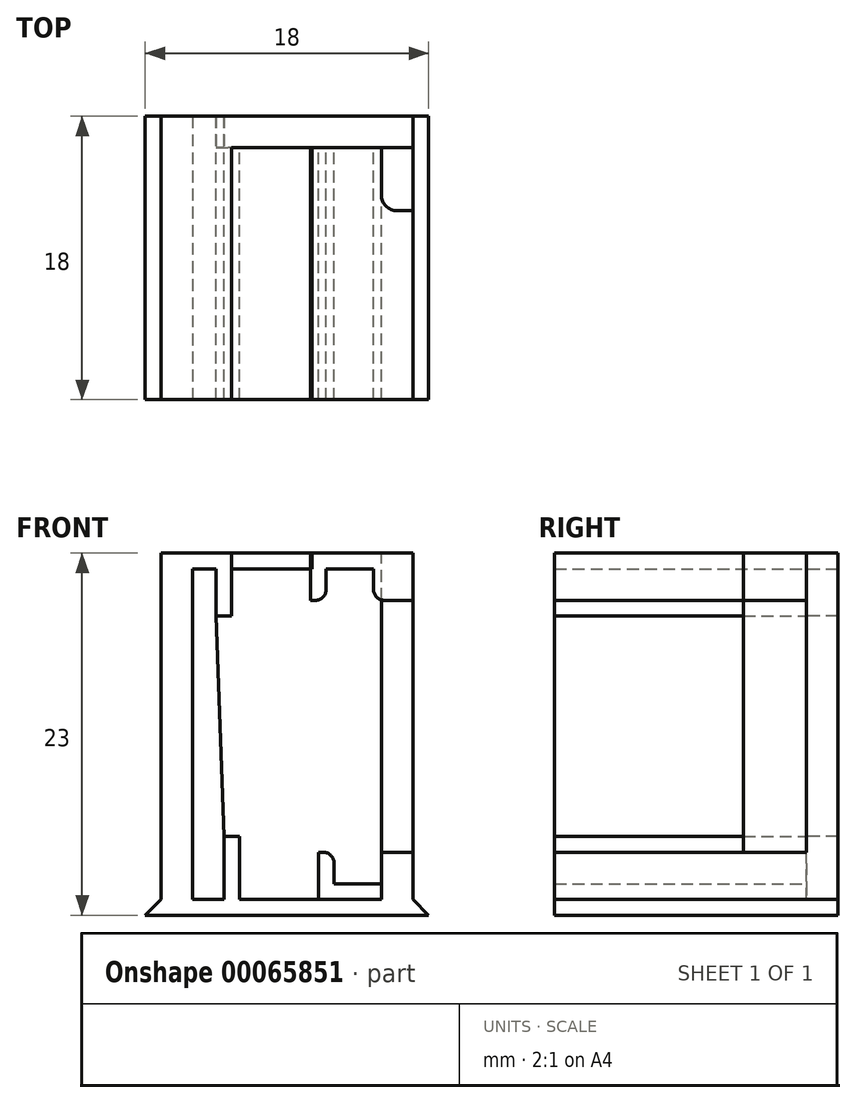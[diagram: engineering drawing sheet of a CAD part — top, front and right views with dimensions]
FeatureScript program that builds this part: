
annotation { "Feature Type Name" : "Feature", "Feature Type Description" : "" }
export const myFeature = defineFeature(function(context is Context, id is Id, definition is map)
    precondition{}
    {
        {
            var Q0;
            Q0=qCreatedBy(makeId("Top.planeOp"),FACE);
            var sketch = newSketch(context, id + "F0", { "sketchPlane" : qUnion([Q0])});
            skLineSegment(sketch, "E0.bottom", {"start": v(9, -10.06) * mm, "end": v(-9, -10.06) * mm});
            skLineSegment(sketch, "E0.left", {"start": v(9, -10.06) * mm, "end": v(9, 7.94) * mm});
            skLineSegment(sketch, "E0.right", {"start": v(-9, -10.06) * mm, "end": v(-9, 7.94) * mm});
            skPoint(sketch, "E0.middle", {"position": v(0, 0) * mm});
            skPoint(sketch, "E1.orphan", {"position": v(-9, 10.06) * mm});
            skPoint(sketch, "E2.orphan", {"position": v(9, 10.06) * mm});
            skLineSegment(sketch, "E3", {"start": v(9, 7.94) * mm, "end": v(-9, 7.94) * mm});
            skSolve(sketch);
        }
        {
            var Q0;
            Q0 = qSketchRegion(id + "F0", true);
            extrude(context, id + "F1", {"entities" : qUnion([Q0]), "depth" : 1 * mm});
        }
        {
            var Q0;
            Q0=makeQuery(id+"F1.opExtrude","CAP_FACE",FACE,{"disambiguationData":[OSD([sQuery(id+"F0.wireOp",EDGE,"E0.bottom"),sQuery(id+"F0.wireOp",EDGE,"E0.top"),sQuery(id+"F0.wireOp",EDGE,"E0.left"),sQuery(id+"F0.wireOp",EDGE,"E0.right")])],"isStart":false});
            var sketch = newSketch(context, id + "F2", { "sketchPlane" : qUnion([Q0])});
            skLineSegment(sketch, "E4.bottom", {"start": v(8, -10.06) * mm, "end": v(-8, -10.06) * mm});
            skLineSegment(sketch, "E4.top", {"start": v(8, 7.94) * mm, "end": v(-8, 7.94) * mm});
            skLineSegment(sketch, "E4.left", {"start": v(8, -10.06) * mm, "end": v(8, 7.94) * mm});
            skLineSegment(sketch, "E4.right", {"start": v(-8, -10.06) * mm, "end": v(-8, 7.94) * mm});
            skPoint(sketch, "E4.middle", {"position": v(0, -1.06) * mm});
            skLineSegment(sketch, "E5.bottom", {"start": v(-6, 5.94) * mm, "end": v(6, 5.94) * mm});
            skLineSegment(sketch, "E5.top", {"start": v(-6, -10.06) * mm, "end": v(6, -10.06) * mm});
            skLineSegment(sketch, "E5.left", {"start": v(-6, 5.94) * mm, "end": v(-6, -10.06) * mm});
            skLineSegment(sketch, "E5.right", {"start": v(6, 5.94) * mm, "end": v(6, -10.06) * mm});
            skSolve(sketch);
        }
        {
            var Q0;
            Q0=makeQuery(id+"F2.imprint","IMPRINT",FACE,{"disambiguationData":[TD([[makeQuery(id+"F2.imprint","IMPRINT",EDGE,{"derivedFrom":sQuery(id+"F2.wireOp",EDGE,"E4.top")}),1.0]])]});
            extrude(context, id + "F3", {"entities" : qUnion([Q0]), "operationType" : NewBodyOperationType.ADD, "depth" : 22 * mm});
        }
        {
            var Q0;
            {var subQ0=sQuery(id+"F2.wireOp",EDGE,"E4.bottom");var subQ1=sQuery(id+"F0.wireOp",EDGE,"E0.bottom");var subQ2=makeQuery(id+"F1.opExtrude","CAP_EDGE",EDGE,{"disambiguationData":[OSD([subQ1])],"isStart":false});Q0=makeQuery(id+"F3.boolean.opBoolean","MERGE",FACE,{"derivedFrom":[makeQuery(id+"F1.opExtrude","SWEPT_FACE",FACE,{"disambiguationData":[OSD([subQ1])]}),makeQuery(id+"F3.opExtrude","SWEPT_FACE",FACE,{"disambiguationData":[OSD([subQ0]),TDD([makeQuery(id+"F2.imprint","IMPRINT",EDGE,{"disambiguationData":[TD([[makeQuery(id+"F2.imprint","INTERSECT",VERTEX,{"derivedFrom":[subQ2,subQ0,sQuery(id+"F2.wireOp",EDGE,"E4.left")]}),-1.0]])],"derivedFrom":subQ0})])]}),makeQuery(id+"F3.opExtrude","SWEPT_FACE",FACE,{"disambiguationData":[OSD([subQ0]),TDD([makeQuery(id+"F2.imprint","IMPRINT",EDGE,{"disambiguationData":[TD([[makeQuery(id+"F2.imprint","INTERSECT",VERTEX,{"derivedFrom":[subQ2,subQ0,sQuery(id+"F2.wireOp",EDGE,"E4.right")]}),1.0]])],"derivedFrom":subQ0})])]})]});}
            var sketch = newSketch(context, id + "F4", { "sketchPlane" : qUnion([Q0])});
            skLineSegment(sketch, "E6", {"start": v(-9, 0) * mm, "end": v(-8, 1) * mm});
            skLineSegment(sketch, "E7", {"start": v(9, 0) * mm, "end": v(8, 1) * mm});
            skSolve(sketch);
        }
        {
            var Q0;
            Q0=makeQuery(id+"F4.imprint","IMPRINT",FACE,{"disambiguationData":[TD([[makeQuery(id+"F4.imprint","IMPRINT",EDGE,{"derivedFrom":sQuery(id+"F4.wireOp",EDGE,"E6")}),1.0]])]});
            var Q1;
            Q1=makeQuery(id+"F1.opExtrude","CAP_EDGE",EDGE,{"disambiguationData":[OSD([sQuery(id+"F0.wireOp",EDGE,"E0.right")])],"isStart":true});
            sweep(context, id + "F5", {"operationType" : NewBodyOperationType.REMOVE, "profiles" : qUnion([Q0]), "path" : qUnion([Q1])});
        }
        {
            var Q0;
            {var subQ0=sQuery(id+"F2.wireOp",EDGE,"E4.bottom");var subQ1=sQuery(id+"F0.wireOp",EDGE,"E0.bottom");var subQ2=makeQuery(id+"F1.opExtrude","CAP_EDGE",EDGE,{"disambiguationData":[OSD([subQ1])],"isStart":false});Q0=makeQuery(id+"F3.boolean.opBoolean","MERGE",FACE,{"derivedFrom":[makeQuery(id+"F1.opExtrude","SWEPT_FACE",FACE,{"disambiguationData":[OSD([subQ1])]}),makeQuery(id+"F3.opExtrude","SWEPT_FACE",FACE,{"disambiguationData":[OSD([subQ0]),TDD([makeQuery(id+"F2.imprint","IMPRINT",EDGE,{"disambiguationData":[TD([[makeQuery(id+"F2.imprint","INTERSECT",VERTEX,{"derivedFrom":[subQ2,subQ0,sQuery(id+"F2.wireOp",EDGE,"E4.left")]}),-1.0]])],"derivedFrom":subQ0})])]}),makeQuery(id+"F3.opExtrude","SWEPT_FACE",FACE,{"disambiguationData":[OSD([subQ0]),TDD([makeQuery(id+"F2.imprint","IMPRINT",EDGE,{"disambiguationData":[TD([[makeQuery(id+"F2.imprint","INTERSECT",VERTEX,{"derivedFrom":[subQ2,subQ0,sQuery(id+"F2.wireOp",EDGE,"E4.right")]}),1.0]])],"derivedFrom":subQ0})])]})]});}
            var sketch = newSketch(context, id + "F6", { "sketchPlane" : qUnion([Q0])});
            skLineSegment(sketch, "E8", {"start": v(6, 4) * mm, "end": v(8, 4) * mm});
            skSolve(sketch);
        }
        {
            var Q0;
            Q0 = qSketchRegion(id + "F6", true);
            var Q1;
            {var subQ0=sQuery(id+"F6.wireOp",EDGE,"E8");Q1=makeQuery(id+"F6.imprint","IMPRINT",FACE,{"disambiguationData":[TD([[makeQuery(id+"F6.imprint","IMPRINT",EDGE,{"derivedFrom":subQ0}),1.0]])]});}
            var Q2;
            Q2=makeQuery(id+"F3.opExtrude","SWEPT_FACE",FACE,{"disambiguationData":[OSD([sQuery(id+"F2.wireOp",EDGE,"E5.bottom")])]});
            extrude(context, id + "F7", {"entities" : qUnion([Q0, Q1]), "operationType" : NewBodyOperationType.REMOVE, "endBound" : BoundingType.UP_TO_SURFACE, "oppositeDirection" : true, "endBoundEntityFace" : qUnion([Q2]), "depth" : 25 * mm});
        }
        {
            var Q0;
            Q0=makeQuery(id+"F7.boolean.opBoolean","MERGE",FACE,{"derivedFrom":[makeQuery(id+"F3.opExtrude","SWEPT_FACE",FACE,{"disambiguationData":[OSD([sQuery(id+"F2.wireOp",EDGE,"E5.bottom")])]})],"fromTools":[makeQuery(id+"F7.opExtrude","CAP_FACE",FACE,{"disambiguationData":[OSD([sQuery(id+"F0.wireOp",EDGE,"E0.bottom"),sQuery(id+"F2.wireOp",EDGE,"E4.bottom"),sQuery(id+"F2.wireOp",EDGE,"E4.left"),sQuery(id+"F2.wireOp",EDGE,"E5.top"),sQuery(id+"F2.wireOp",EDGE,"E5.right"),sQuery(id+"F6.wireOp",EDGE,"E8")])],"isStart":false})]});
            var sketch = newSketch(context, id + "F8", { "sketchPlane" : qUnion([Q0])});
            skLineSegment(sketch, "E9.bottom", {"start": v(-6, 23) * mm, "end": v(-3.5, 23) * mm});
            skLineSegment(sketch, "E9.top", {"start": v(-6, 19) * mm, "end": v(-6, 19) * mm});
            skLineSegment(sketch, "E9.left", {"start": v(-6, 23) * mm, "end": v(-6, 19) * mm});
            skLineSegment(sketch, "E9.right", {"start": v(-3.5, 23) * mm, "end": v(-3.5, 19) * mm});
            skLineSegment(sketch, "E10.top", {"start": v(-6, 22) * mm, "end": v(-4.5, 22) * mm});
            skLineSegment(sketch, "E10.left", {"start": v(-6, 19) * mm, "end": v(-6, 22) * mm});
            skLineSegment(sketch, "E10.right", {"start": v(-4.5, 19) * mm, "end": v(-4.5, 22) * mm});
            skLineSegment(sketch, "E11.bottom", {"start": v(-3, 1) * mm, "end": v(-5.5, 1) * mm});
            skLineSegment(sketch, "E11.top", {"start": v(-3, 5) * mm, "end": v(-4, 5) * mm});
            skLineSegment(sketch, "E11.left", {"start": v(-3, 1) * mm, "end": v(-3, 5) * mm});
            skLineSegment(sketch, "E11.right", {"start": v(-5.5, 1) * mm, "end": v(-5.5, 5) * mm});
            skLineSegment(sketch, "E12.top", {"start": v(-4, 1) * mm, "end": v(-5.5, 1) * mm});
            skLineSegment(sketch, "E12.left", {"start": v(-4, 5.19) * mm, "end": v(-4, 1) * mm});
            skLineSegment(sketch, "E12.right", {"start": v(-5.5, 5) * mm, "end": v(-5.5, 1) * mm});
            skLineSegment(sketch, "E13.trimOffspring", {"start": v(-5.5, 5) * mm, "end": v(-5.5, 5) * mm});
            skLineSegment(sketch, "E14.trimOffspring", {"start": v(-4.5, 19) * mm, "end": v(-3.5, 19) * mm});
            skPoint(sketch, "E12.bottom.start.orphan", {"position": v(-4.25, 5) * mm});
            skLineSegment(sketch, "E15", {"start": v(-4, 5.19) * mm, "end": v(-4, 5) * mm});
            skSolve(sketch);
        }
        {
            var Q0;
            Q0=makeQuery(id+"F8.imprint","IMPRINT",FACE,{"disambiguationData":[TD([[makeQuery(id+"F8.imprint","IMPRINT",EDGE,{"derivedFrom":sQuery(id+"F8.wireOp",EDGE,"E9.bottom")}),-1.0]])]});
            var Q1;
            Q1=makeQuery(id+"F8.imprint","IMPRINT",FACE,{"disambiguationData":[TD([[makeQuery(id+"F8.imprint","IMPRINT",EDGE,{"derivedFrom":sQuery(id+"F8.wireOp",EDGE,"E11.bottom")}),1.0]])]});
            var Q2;
            {var subQ0=sQuery(id+"F2.wireOp",EDGE,"E4.bottom");var subQ1=sQuery(id+"F0.wireOp",EDGE,"E0.bottom");var subQ2=makeQuery(id+"F1.opExtrude","CAP_EDGE",EDGE,{"disambiguationData":[OSD([subQ1])],"isStart":false});Q2=makeQuery(id+"F3.boolean.opBoolean","MERGE",FACE,{"derivedFrom":[makeQuery(id+"F1.opExtrude","SWEPT_FACE",FACE,{"disambiguationData":[OSD([subQ1])]}),makeQuery(id+"F3.opExtrude","SWEPT_FACE",FACE,{"disambiguationData":[OSD([subQ0]),TDD([makeQuery(id+"F2.imprint","IMPRINT",EDGE,{"disambiguationData":[TD([[makeQuery(id+"F2.imprint","INTERSECT",VERTEX,{"derivedFrom":[subQ2,subQ0,sQuery(id+"F2.wireOp",EDGE,"E4.left")]}),-1.0]])],"derivedFrom":subQ0})])]}),makeQuery(id+"F3.opExtrude","SWEPT_FACE",FACE,{"disambiguationData":[OSD([subQ0]),TDD([makeQuery(id+"F2.imprint","IMPRINT",EDGE,{"disambiguationData":[TD([[makeQuery(id+"F2.imprint","INTERSECT",VERTEX,{"derivedFrom":[subQ2,subQ0,sQuery(id+"F2.wireOp",EDGE,"E4.right")]}),1.0]])],"derivedFrom":subQ0})])]})]});}
            extrude(context, id + "F9", {"entities" : qUnion([Q0, Q1]), "operationType" : NewBodyOperationType.ADD, "endBound" : BoundingType.UP_TO_SURFACE, "endBoundEntityFace" : qUnion([Q2]), "depth" : 25 * mm});
        }
        {
            var Q0;
            Q0=makeQuery(id+"F4.imprint","IMPRINT",FACE,{"disambiguationData":[TD([[makeQuery(id+"F4.imprint","IMPRINT",EDGE,{"derivedFrom":sQuery(id+"F4.wireOp",EDGE,"E7")}),-1.0]])]});
            extrude(context, id + "F10", {"entities" : qUnion([Q0]), "operationType" : NewBodyOperationType.REMOVE, "oppositeDirection" : true, "depth" : 25 * mm});
        }
        {
            var Q0;
            Q0=makeQuery(id+"F7.boolean.opBoolean","MERGE",FACE,{"derivedFrom":[makeQuery(id+"F3.opExtrude","SWEPT_FACE",FACE,{"disambiguationData":[OSD([sQuery(id+"F2.wireOp",EDGE,"E5.bottom")])]})],"fromTools":[makeQuery(id+"F7.opExtrude","CAP_FACE",FACE,{"disambiguationData":[OSD([sQuery(id+"F0.wireOp",EDGE,"E0.bottom"),sQuery(id+"F2.wireOp",EDGE,"E4.bottom"),sQuery(id+"F2.wireOp",EDGE,"E4.left"),sQuery(id+"F2.wireOp",EDGE,"E5.top"),sQuery(id+"F2.wireOp",EDGE,"E5.right"),sQuery(id+"F6.wireOp",EDGE,"E8")])],"isStart":false})]});
            var sketch = newSketch(context, id + "F11", { "sketchPlane" : qUnion([Q0])});
            skLineSegment(sketch, "E16.bottom", {"start": v(6, 1) * mm, "end": v(2, 1) * mm});
            skLineSegment(sketch, "E16.top", {"start": v(6, 4) * mm, "end": v(6, 4) * mm});
            skLineSegment(sketch, "E16.left", {"start": v(6, 1) * mm, "end": v(6, 4) * mm});
            skLineSegment(sketch, "E16.right", {"start": v(2, 1) * mm, "end": v(2, 4) * mm});
            skLineSegment(sketch, "E17.top", {"start": v(3, 2) * mm, "end": v(6, 2) * mm});
            skLineSegment(sketch, "E17.left", {"start": v(3, 4) * mm, "end": v(3, 2) * mm});
            skLineSegment(sketch, "E17.right", {"start": v(6, 4) * mm, "end": v(6, 2) * mm});
            skLineSegment(sketch, "E18.bottom", {"start": v(5.5, 23) * mm, "end": v(1.5, 23) * mm});
            skLineSegment(sketch, "E18.top", {"start": v(5.5, 20) * mm, "end": v(5.5, 20) * mm});
            skLineSegment(sketch, "E18.left", {"start": v(5.5, 22) * mm, "end": v(5.5, 20) * mm});
            skLineSegment(sketch, "E18.right", {"start": v(1.5, 23) * mm, "end": v(1.5, 20) * mm});
            skLineSegment(sketch, "E19.top", {"start": v(2.5, 22) * mm, "end": v(5.5, 22) * mm});
            skLineSegment(sketch, "E19.left", {"start": v(2.5, 20) * mm, "end": v(2.5, 22) * mm});
            skLineSegment(sketch, "E19.right", {"start": v(5.5, 20) * mm, "end": v(5.5, 22) * mm});
            skLineSegment(sketch, "E20.trimOffspring", {"start": v(2.5, 20) * mm, "end": v(1.5, 20) * mm});
            skLineSegment(sketch, "E21.trimOffspring", {"start": v(3, 4) * mm, "end": v(2, 4) * mm});
            skLineSegment(sketch, "E22", {"start": v(5.5, 20) * mm, "end": v(8, 20) * mm});
            skLineSegment(sketch, "E23", {"start": v(1.5, 23) * mm, "end": v(8, 23) * mm});
            skLineSegment(sketch, "E24", {"start": v(8, 23) * mm, "end": v(8, 20) * mm});
            skSolve(sketch);
        }
        {
            var Q0;
            Q0 = qSketchRegion(id + "F11", true);
            var Q1;
            {var subQ0=sQuery(id+"F2.wireOp",EDGE,"E4.bottom");var subQ1=sQuery(id+"F0.wireOp",EDGE,"E0.bottom");var subQ2=makeQuery(id+"F1.opExtrude","CAP_EDGE",EDGE,{"disambiguationData":[OSD([subQ1])],"isStart":false});Q1=makeQuery(id+"F3.boolean.opBoolean","MERGE",FACE,{"derivedFrom":[makeQuery(id+"F1.opExtrude","SWEPT_FACE",FACE,{"disambiguationData":[OSD([subQ1])]}),makeQuery(id+"F3.opExtrude","SWEPT_FACE",FACE,{"disambiguationData":[OSD([subQ0]),TDD([makeQuery(id+"F2.imprint","IMPRINT",EDGE,{"disambiguationData":[TD([[makeQuery(id+"F2.imprint","INTERSECT",VERTEX,{"derivedFrom":[subQ2,subQ0,sQuery(id+"F2.wireOp",EDGE,"E4.left")]}),-1.0]])],"derivedFrom":subQ0})])]}),makeQuery(id+"F3.opExtrude","SWEPT_FACE",FACE,{"disambiguationData":[OSD([subQ0]),TDD([makeQuery(id+"F2.imprint","IMPRINT",EDGE,{"disambiguationData":[TD([[makeQuery(id+"F2.imprint","INTERSECT",VERTEX,{"derivedFrom":[subQ2,subQ0,sQuery(id+"F2.wireOp",EDGE,"E4.right")]}),1.0]])],"derivedFrom":subQ0})])]})]});}
            extrude(context, id + "F12", {"entities" : qUnion([Q0]), "endBound" : BoundingType.UP_TO_SURFACE, "endBoundEntityFace" : qUnion([Q1]), "depth" : 20 * mm});
        }
        {
            var Q0;
            Q0=makeQuery(id+"F7.boolean.opBoolean","MERGE",FACE,{"derivedFrom":[makeQuery(id+"F3.opExtrude","SWEPT_FACE",FACE,{"disambiguationData":[OSD([sQuery(id+"F2.wireOp",EDGE,"E5.bottom")])]})],"fromTools":[makeQuery(id+"F7.opExtrude","CAP_FACE",FACE,{"disambiguationData":[OSD([sQuery(id+"F0.wireOp",EDGE,"E0.bottom"),sQuery(id+"F2.wireOp",EDGE,"E4.bottom"),sQuery(id+"F2.wireOp",EDGE,"E4.left"),sQuery(id+"F2.wireOp",EDGE,"E5.top"),sQuery(id+"F2.wireOp",EDGE,"E5.right"),sQuery(id+"F6.wireOp",EDGE,"E8")])],"isStart":false})]});
            var sketch = newSketch(context, id + "F13", { "sketchPlane" : qUnion([Q0])});
            skLineSegment(sketch, "E25.bottom", {"start": v(8, 4) * mm, "end": v(6, 4) * mm});
            skLineSegment(sketch, "E25.top", {"start": v(8, 23) * mm, "end": v(6, 23) * mm});
            skLineSegment(sketch, "E25.left", {"start": v(8, 4) * mm, "end": v(8, 23) * mm});
            skLineSegment(sketch, "E25.right", {"start": v(6, 4) * mm, "end": v(6, 23) * mm});
            skSolve(sketch);
        }
        {
            var Q0;
            Q0 = qSketchRegion(id + "F13", true);
            extrude(context, id + "F14", {"entities" : qUnion([Q0]), "depth" : 2 * mm});
        }
        {
            var Q0;
            Q0=makeQuery(id+"F14.opExtrude","SWEPT_BODY",BODY,{"disambiguationData":[OSD([sQuery(id+"F13.wireOp",EDGE,"E25.bottom"),sQuery(id+"F13.wireOp",EDGE,"E25.top"),sQuery(id+"F13.wireOp",EDGE,"E25.left"),sQuery(id+"F13.wireOp",EDGE,"E25.right")])]});
            deleteBodies(context, id + "F15", {"entities" : qUnion([Q0])});
        }
        {
            var Q0;
            Q0 = qSketchRegion(id + "F13", true);
            extrude(context, id + "F16", {"entities" : qUnion([Q0]), "depth" : 4 * mm});
        }
        {
            var Q0;
            Q0=makeQuery(id+"F7.boolean.opBoolean","COPY",EDGE,{"derivedFrom":makeQuery(id+"F7.opExtrude","SWEPT_EDGE",EDGE,{"disambiguationData":[OSD([sQuery(id+"F2.wireOp",EDGE,"E4.bottom"),sQuery(id+"F2.wireOp",EDGE,"E5.top"),sQuery(id+"F2.wireOp",EDGE,"E5.right"),sQuery(id+"F6.wireOp",EDGE,"E8")])]})});
            var Q1;
            Q1=makeQuery(id+"F12.opExtrude","SWEPT_EDGE",EDGE,{"disambiguationData":[OSD([sQuery(id+"F11.wireOp",EDGE,"E17.left"),sQuery(id+"F11.wireOp",EDGE,"E21.trimOffspring")])]});
            var Q2;
            Q2=makeQuery(id+"F12.opExtrude","SWEPT_EDGE",EDGE,{"disambiguationData":[OSD([sQuery(id+"F11.wireOp",EDGE,"E19.left"),sQuery(id+"F11.wireOp",EDGE,"E20.trimOffspring")])]});
            var Q3;
            Q3=makeQuery(id+"F12.opExtrude","SWEPT_EDGE",EDGE,{"disambiguationData":[OSD([sQuery(id+"F11.wireOp",EDGE,"E19.right"),sQuery(id+"F11.wireOp",EDGE,"E22")])]});
            fillet(context, id + "F17", {"entities" : qUnion([Q0, Q1, Q2, Q3]), "radius" : .7 * mm, "tangentPropagation" : true, "allowEdgeOverflow" : false});
        }
        {
            var Q0;
            Q0=makeQuery(id+"F16.opExtrude","CAP_EDGE",EDGE,{"disambiguationData":[OSD([sQuery(id+"F13.wireOp",EDGE,"E25.right")])],"isStart":false});
            fillet(context, id + "F18", {"entities" : qUnion([Q0]), "radius" : 1 * mm, "tangentPropagation" : true, "allowEdgeOverflow" : false});
        }
        {
            var Q0;
            Q0=makeQuery(id+"F7.boolean.opBoolean","MERGE",FACE,{"derivedFrom":[makeQuery(id+"F3.opExtrude","SWEPT_FACE",FACE,{"disambiguationData":[OSD([sQuery(id+"F2.wireOp",EDGE,"E5.bottom")])]})],"fromTools":[makeQuery(id+"F7.opExtrude","CAP_FACE",FACE,{"disambiguationData":[OSD([sQuery(id+"F0.wireOp",EDGE,"E0.bottom"),sQuery(id+"F2.wireOp",EDGE,"E4.bottom"),sQuery(id+"F2.wireOp",EDGE,"E4.left"),sQuery(id+"F2.wireOp",EDGE,"E5.top"),sQuery(id+"F2.wireOp",EDGE,"E5.right"),sQuery(id+"F6.wireOp",EDGE,"E8")])],"isStart":false})]});
            var sketch = newSketch(context, id + "F19", { "sketchPlane" : qUnion([Q0])});
            skLineSegment(sketch, "E26", {"start": v(-3.5, 22) * mm, "end": v(1.6, 22) * mm});
            skLineSegment(sketch, "E27.bottom", {"start": v(-3.5, 23) * mm, "end": v(1.6, 23) * mm});
            skLineSegment(sketch, "E27.left", {"start": v(-3.5, 23) * mm, "end": v(-3.5, 22) * mm});
            skLineSegment(sketch, "E27.right", {"start": v(1.6, 23) * mm, "end": v(1.6, 22) * mm});
            skSolve(sketch);
        }
        {
            var Q0;
            Q0 = qSketchRegion(id + "F19", true);
            var Q1;
            {var subQ0=sQuery(id+"F2.wireOp",EDGE,"E4.bottom");var subQ1=sQuery(id+"F0.wireOp",EDGE,"E0.bottom");var subQ2=makeQuery(id+"F1.opExtrude","CAP_EDGE",EDGE,{"disambiguationData":[OSD([subQ1])],"isStart":false});Q1=makeQuery(id+"F9.boolean.opBoolean","MERGE",FACE,{"derivedFrom":[makeQuery(id+"F3.boolean.opBoolean","MERGE",FACE,{"derivedFrom":[makeQuery(id+"F1.opExtrude","SWEPT_FACE",FACE,{"disambiguationData":[OSD([subQ1])]}),makeQuery(id+"F3.opExtrude","SWEPT_FACE",FACE,{"disambiguationData":[OSD([subQ0]),TDD([makeQuery(id+"F2.imprint","IMPRINT",EDGE,{"disambiguationData":[TD([[makeQuery(id+"F2.imprint","INTERSECT",VERTEX,{"derivedFrom":[subQ2,subQ0,sQuery(id+"F2.wireOp",EDGE,"E4.left")]}),-1.0]])],"derivedFrom":subQ0})])]}),makeQuery(id+"F3.opExtrude","SWEPT_FACE",FACE,{"disambiguationData":[OSD([subQ0]),TDD([makeQuery(id+"F2.imprint","IMPRINT",EDGE,{"disambiguationData":[TD([[makeQuery(id+"F2.imprint","INTERSECT",VERTEX,{"derivedFrom":[subQ2,subQ0,sQuery(id+"F2.wireOp",EDGE,"E4.right")]}),1.0]])],"derivedFrom":subQ0})])]})]}),makeQuery(id+"F9.opExtrude","CAP_FACE",FACE,{"disambiguationData":[OSD([sQuery(id+"F8.wireOp",EDGE,"E9.bottom"),sQuery(id+"F8.wireOp",EDGE,"E9.left"),sQuery(id+"F8.wireOp",EDGE,"E9.right"),sQuery(id+"F8.wireOp",EDGE,"E10.top"),sQuery(id+"F8.wireOp",EDGE,"E10.right"),sQuery(id+"F8.wireOp",EDGE,"E14.trimOffspring")])],"isStart":false}),makeQuery(id+"F9.opExtrude","CAP_FACE",FACE,{"disambiguationData":[OSD([sQuery(id+"F8.wireOp",EDGE,"E11.bottom"),sQuery(id+"F8.wireOp",EDGE,"E11.top"),sQuery(id+"F8.wireOp",EDGE,"E11.left"),sQuery(id+"F8.wireOp",EDGE,"E12.left")])],"isStart":false})]});}
            extrude(context, id + "F20", {"entities" : qUnion([Q0]), "endBound" : BoundingType.UP_TO_SURFACE, "endBoundEntityFace" : qUnion([Q1]), "depth" : 25 * mm});
        }
        {
            var Q0;
            Q0=makeQuery(id+"F7.boolean.opBoolean","MERGE",FACE,{"derivedFrom":[makeQuery(id+"F3.opExtrude","SWEPT_FACE",FACE,{"disambiguationData":[OSD([sQuery(id+"F2.wireOp",EDGE,"E5.bottom")])]})],"fromTools":[makeQuery(id+"F7.opExtrude","CAP_FACE",FACE,{"disambiguationData":[OSD([sQuery(id+"F0.wireOp",EDGE,"E0.bottom"),sQuery(id+"F2.wireOp",EDGE,"E4.bottom"),sQuery(id+"F2.wireOp",EDGE,"E4.left"),sQuery(id+"F2.wireOp",EDGE,"E5.top"),sQuery(id+"F2.wireOp",EDGE,"E5.right"),sQuery(id+"F6.wireOp",EDGE,"E8")])],"isStart":false})]});
            var sketch = newSketch(context, id + "F21", { "sketchPlane" : qUnion([Q0])});
            skLineSegment(sketch, "E28", {"start": v(-4, 5) * mm, "end": v(-4.5, 19) * mm});
            skSolve(sketch);
        }
        {
            var Q0;
            Q0=makeQuery(id+"F21.imprint","IMPRINT",FACE,{"disambiguationData":[TD([[makeQuery(id+"F21.imprint","IMPRINT",EDGE,{"derivedFrom":sQuery(id+"F21.wireOp",EDGE,"E28")}),1.0]])]});
            extrude(context, id + "F22", {"entities" : qUnion([Q0]), "operationType" : NewBodyOperationType.REMOVE, "oppositeDirection" : true, "depth" : 25 * mm});
        }
    });
